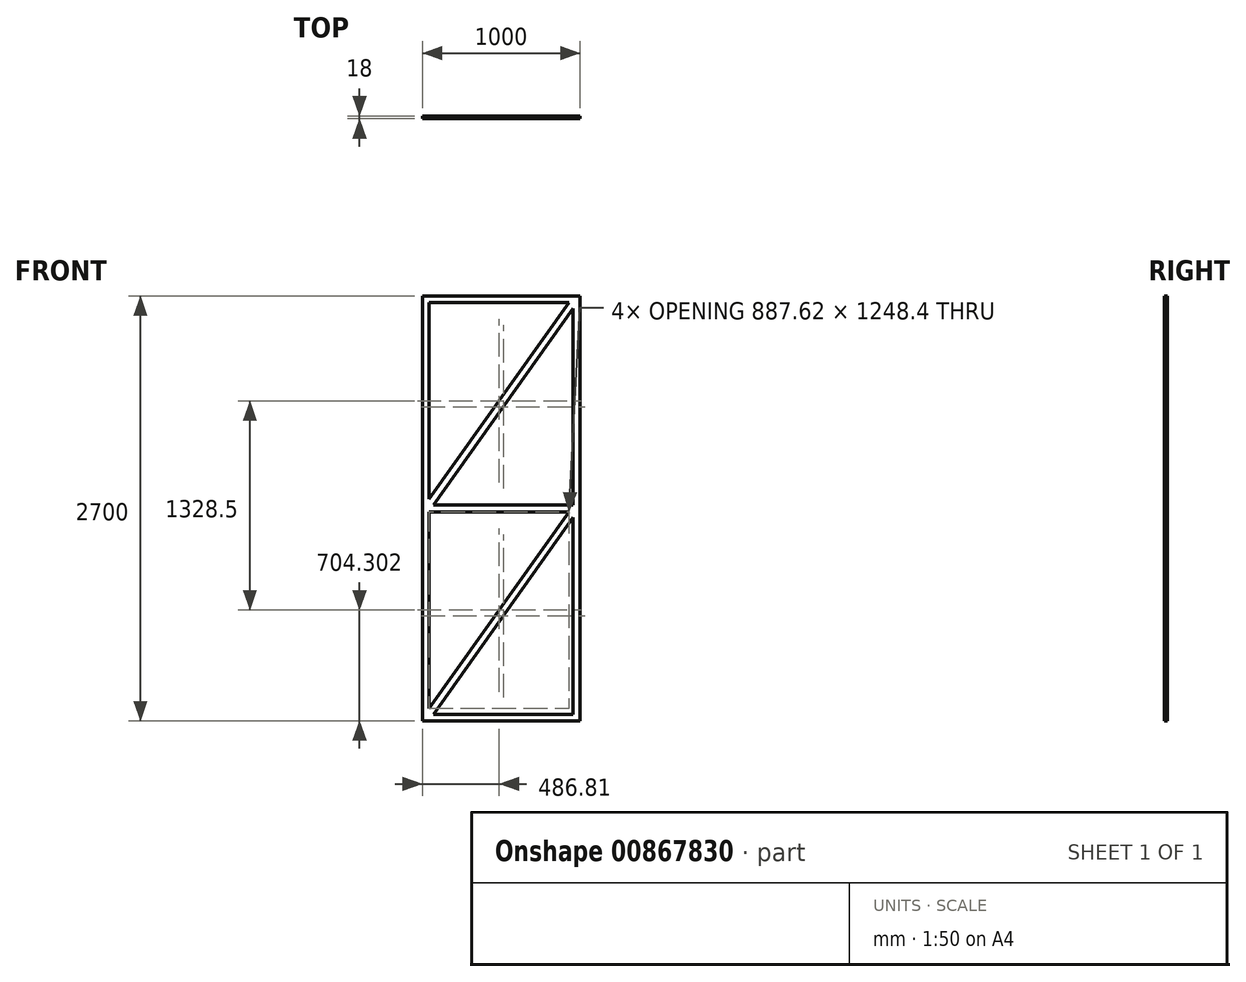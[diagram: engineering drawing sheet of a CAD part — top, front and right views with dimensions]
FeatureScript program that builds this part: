
annotation { "Feature Type Name" : "Feature", "Feature Type Description" : "" }
export const myFeature = defineFeature(function(context is Context, id is Id, definition is map)
    precondition{}
    {
        {
            var Q0;
            Q0=qCreatedBy(makeId("Front.planeOp"),FACE);
            var sketch = newSketch(context, id + "F0", { "sketchPlane" : qUnion([Q0])});
            skLineSegment(sketch, "E0.bottom", {"start": v(-500, 1350) * mm, "end": v(500, 1350) * mm});
            skLineSegment(sketch, "E0.top", {"start": v(-500, -1350) * mm, "end": v(500, -1350) * mm});
            skLineSegment(sketch, "E0.left", {"start": v(-500, 1350) * mm, "end": v(-500, -1350) * mm});
            skLineSegment(sketch, "E0.right", {"start": v(500, 1350) * mm, "end": v(500, -1350) * mm});
            skPoint(sketch, "E0.middle", {"position": v(0, 0) * mm});
            skLineSegment(sketch, "E1.bottom", {"start": v(-457, 1307) * mm, "end": v(457, 1307) * mm});
            skLineSegment(sketch, "E1.top", {"start": v(-457, -1307) * mm, "end": v(457, -1307) * mm});
            skLineSegment(sketch, "E1.left", {"start": v(-457, 1307) * mm, "end": v(-457, -1307) * mm});
            skLineSegment(sketch, "E1.right", {"start": v(457, 1307) * mm, "end": v(457, -1307) * mm});
            skLineSegment(sketch, "E2", {"start": v(-457, 0) * mm, "end": v(457, 0) * mm, "construction": true});
            skLineSegment(sketch, "E3.bottom", {"start": v(457, 21.5) * mm, "end": v(-457, 21.5) * mm});
            skLineSegment(sketch, "E3.top", {"start": v(457, -21.5) * mm, "end": v(-457, -21.5) * mm});
            skLineSegment(sketch, "E3.left", {"start": v(457, 21.5) * mm, "end": v(457, -21.5) * mm});
            skLineSegment(sketch, "E3.right", {"start": v(-457, 21.5) * mm, "end": v(-457, -21.5) * mm});
            skLineSegment(sketch, "E4", {"start": v(457, 1307) * mm, "end": v(-457, 21.5) * mm, "construction": true});
            skLineSegment(sketch, "E5", {"start": v(457, 1269.9) * mm, "end": v(-430.62, 21.5) * mm});
            skLineSegment(sketch, "E6", {"start": v(430.62, 1307) * mm, "end": v(-457, 58.6) * mm});
            skLineSegment(sketch, "E7", {"start": v(457, -21.5) * mm, "end": v(-457, -1307) * mm, "construction": true});
            skLineSegment(sketch, "E8", {"start": v(457, -58.6) * mm, "end": v(-430.62, -1307) * mm});
            skLineSegment(sketch, "E9", {"start": v(430.62, -21.5) * mm, "end": v(-457, -1269.9) * mm});
            skSolve(sketch);
        }
        {
            var Q0;
            Q0=makeQuery(id+"F0.imprint","IMPRINT",FACE,{"disambiguationData":[TD([[makeQuery(id+"F0.imprint","IMPRINT",EDGE,{"derivedFrom":sQuery(id+"F0.wireOp",EDGE,"E0.bottom")}),-1.0]])]});
            var Q1;
            {var subQ4=sQuery(id+"F0.wireOp",EDGE,"E8");Q1=makeQuery(id+"F0.imprint","IMPRINT",FACE,{"disambiguationData":[TD([[makeQuery(id+"F0.imprint","IMPRINT",EDGE,{"derivedFrom":subQ4}),-1.0]])]});}
            var Q2;
            {var subQ1=sQuery(id+"F0.wireOp",EDGE,"E1.left");var subQ6=sQuery(id+"F0.wireOp",EDGE,"E3.top");var subQ8=makeQuery(id+"F0.imprint","INTERSECT",VERTEX,{"derivedFrom":[subQ1,subQ6]});Q2=makeQuery(id+"F0.imprint","IMPRINT",FACE,{"disambiguationData":[TD([[makeQuery(id+"F0.imprint","IMPRINT",EDGE,{"disambiguationData":[TD([[subQ8,1.0]])],"derivedFrom":subQ1}),1.0]])]});}
            var Q3;
            {var subQ3=sQuery(id+"F0.wireOp",EDGE,"E5");Q3=makeQuery(id+"F0.imprint","IMPRINT",FACE,{"disambiguationData":[TD([[makeQuery(id+"F0.imprint","IMPRINT",EDGE,{"derivedFrom":subQ3}),-1.0]])]});}
            extrude(context, id + "F1", {"entities" : qUnion([Q0, Q1, Q2, Q3]), "depth" : 18 * mm, "offsetDistance" : 25 * mm});
        }
    });
